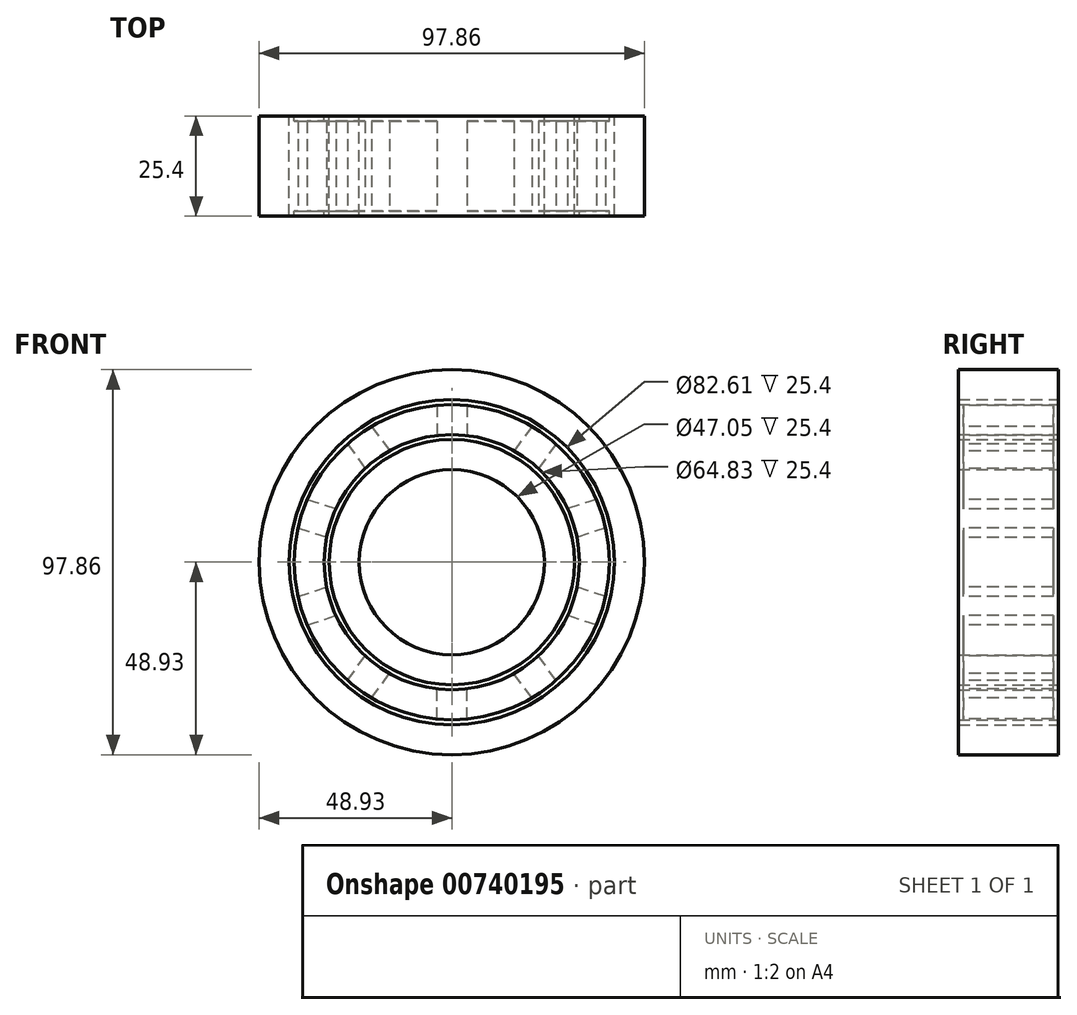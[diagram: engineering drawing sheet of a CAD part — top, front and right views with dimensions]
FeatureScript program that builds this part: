
annotation { "Feature Type Name" : "Feature", "Feature Type Description" : "" }
export const myFeature = defineFeature(function(context is Context, id is Id, definition is map)
    precondition{}
    {
        {
            var Q0;
            Q0=qCreatedBy(makeId("Top.planeOp"),FACE);
            var sketch = newSketch(context, id + "F0", { "sketchPlane" : qUnion([Q0])});
            skLineSegment(sketch, "E0.bottom", {"start": v(-48.93, 17.1) * mm, "end": v(-23.53, 17.1) * mm});
            skLineSegment(sketch, "E0.top", {"start": v(-48.93, -8.3) * mm, "end": v(-23.53, -8.3) * mm});
            skLineSegment(sketch, "E0.left", {"start": v(-48.93, 17.1) * mm, "end": v(-48.93, -8.3) * mm});
            skLineSegment(sketch, "E0.right", {"start": v(-23.53, 17.1) * mm, "end": v(-23.53, -8.3) * mm});
            skLineSegment(sketch, "E1", {"start": v(-41.3, 17.1) * mm, "end": v(-41.3, -8.3) * mm});
            skLineSegment(sketch, "E2", {"start": v(-31.15, 17.1) * mm, "end": v(-31.15, -8.3) * mm});
            skLineSegment(sketch, "E3", {"start": v(0, 17.1) * mm, "end": v(0, 0) * mm});
            skLineSegment(sketch, "E4", {"start": v(-40.04, -7.04) * mm, "end": v(-32.42, -7.04) * mm});
            skLineSegment(sketch, "E5", {"start": v(-40.04, 15.82) * mm, "end": v(-32.42, 15.82) * mm});
            skLineSegment(sketch, "E6", {"start": v(-40.04, 15.82) * mm, "end": v(-40.04, -7.04) * mm});
            skLineSegment(sketch, "E7", {"start": v(-32.42, 15.82) * mm, "end": v(-32.42, -7.04) * mm});
            skLineSegment(sketch, "E8", {"start": v(-40.04, -7.04) * mm, "end": v(-40.04, -8.3) * mm});
            skLineSegment(sketch, "E9", {"start": v(-32.42, -7.04) * mm, "end": v(-32.42, -8.3) * mm});
            skLineSegment(sketch, "E10", {"start": v(-40.04, 15.82) * mm, "end": v(-40.04, 17.1) * mm});
            skLineSegment(sketch, "E11", {"start": v(-32.42, 15.82) * mm, "end": v(-32.42, 17.1) * mm});
            skSolve(sketch);
        }
        {
            var Q0;
            Q0=makeQuery(id+"F0.imprint","IMPRINT",FACE,{"disambiguationData":[TD([[makeQuery(id+"F0.imprint","IMPRINT",EDGE,{"derivedFrom":sQuery(id+"F0.wireOp",EDGE,"E5")}),1.0]])]});
            var Q1;
            Q1=makeQuery(id+"F0.imprint","IMPRINT",FACE,{"disambiguationData":[TD([[makeQuery(id+"F0.imprint","IMPRINT",EDGE,{"derivedFrom":sQuery(id+"F0.wireOp",EDGE,"E4")}),-1.0]])]});
            var Q2;
            Q2=sQuery(id+"F0.wireOp",EDGE,"E3");
            revolve(context, id + "F1", {"surfaceOperationType" : NewSurfaceOperationType.NEW, "entities" : qUnion([Q0, Q1]), "axis" : qUnion([Q2]), "revolveType" : RevolveType.FULL});
        }
        {
            var Q0;
            Q0=makeQuery(id+"F1.opRevolve","SWEPT_FACE",FACE,{"disambiguationData":[OSD([sQuery(id+"F0.wireOp",EDGE,"E0.top")])]});
            var sketch = newSketch(context, id + "F2", { "sketchPlane" : qUnion([Q0])});
            skLineSegment(sketch, "E12", {"start": v(-3.8, 39.85) * mm, "end": v(-3.8, 32.2) * mm});
            skLineSegment(sketch, "E13", {"start": v(3.81, 39.85) * mm, "end": v(3.81, 32.2) * mm});
            skSolve(sketch);
        }
        {
            var Q0;
            {var subQ0=sQuery(id+"F2.wireOp",EDGE,"E12");Q0=makeQuery(id+"F2.imprint","IMPRINT",FACE,{"disambiguationData":[TD([[makeQuery(id+"F2.imprint","IMPRINT",EDGE,{"derivedFrom":subQ0}),1.0]])]});}
            extrude(context, id + "F3", {"entities" : qUnion([Q0]), "operationType" : NewBodyOperationType.ADD, "oppositeDirection" : true, "depth" : 25.4 * mm, "offsetDistance" : 25.4 * mm});
        }
        {
            var Q0;
            Q0=makeQuery(id+"F1.opRevolve","SWEPT_BODY",BODY,{"disambiguationData":[OSD([sQuery(id+"F0.wireOp",EDGE,"E0.bottom"),sQuery(id+"F0.wireOp",EDGE,"E5"),sQuery(id+"F0.wireOp",EDGE,"E10"),sQuery(id+"F0.wireOp",EDGE,"E11")])]});
            var Q1;
            Q1=sQuery(id+"F0.wireOp",EDGE,"E3");
            circularPattern(context, id + "F4", {"operationType" : NewBodyOperationType.ADD, "entities" : qUnion([Q0]), "axis" : qUnion([Q1]), "angle" : 360 * degree, "instanceCount" : 10, "equalSpace" : true});
        }
        {
            var Q0;
            {var subQ0=sQuery(id+"F0.wireOp",EDGE,"E0.left");Q0=makeQuery(id+"F0.imprint","IMPRINT",FACE,{"disambiguationData":[TD([[makeQuery(id+"F0.imprint","IMPRINT",EDGE,{"derivedFrom":subQ0}),1.0]])]});}
            var Q1;
            {var subQ0=sQuery(id+"F0.wireOp",EDGE,"E0.right");Q1=makeQuery(id+"F0.imprint","IMPRINT",FACE,{"disambiguationData":[TD([[makeQuery(id+"F0.imprint","IMPRINT",EDGE,{"derivedFrom":subQ0}),-1.0]])]});}
            var Q2;
            Q2=sQuery(id+"F0.wireOp",EDGE,"E3");
            revolve(context, id + "F5", {"surfaceOperationType" : NewSurfaceOperationType.NEW, "entities" : qUnion([Q0, Q1]), "axis" : qUnion([Q2]), "revolveType" : RevolveType.FULL});
        }
    });
